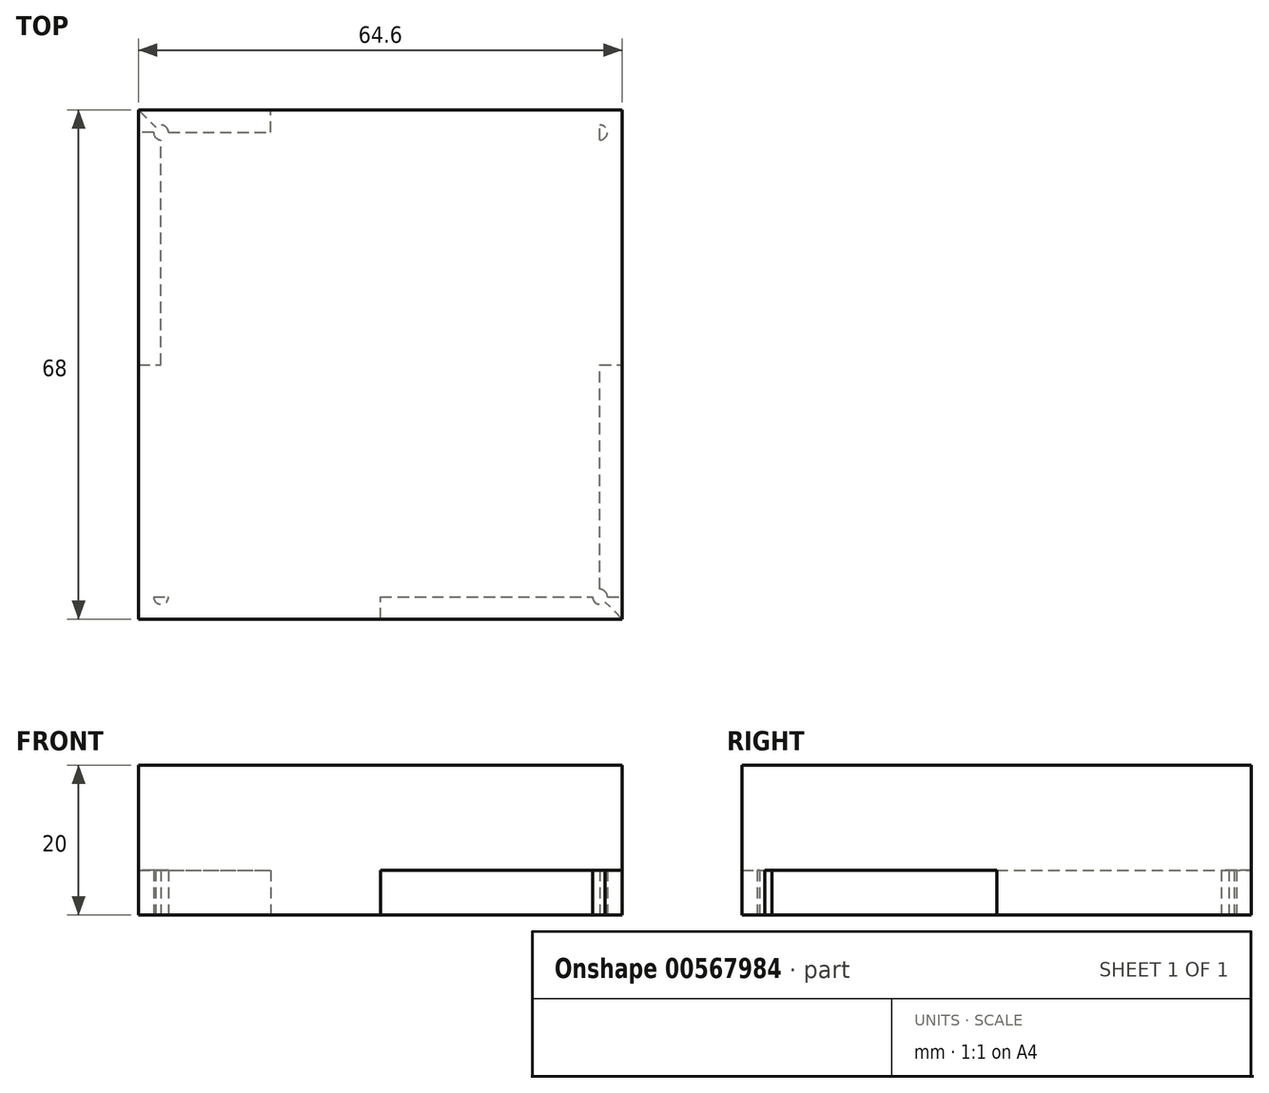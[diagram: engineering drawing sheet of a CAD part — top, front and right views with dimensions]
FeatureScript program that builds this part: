
annotation { "Feature Type Name" : "Feature", "Feature Type Description" : "" }
export const myFeature = defineFeature(function(context is Context, id is Id, definition is map)
    precondition{}
    {
        {
            var Q0;
            Q0=qCreatedBy(makeId("Top.planeOp"),FACE);
            var sketch = newSketch(context, id + "F0", { "sketchPlane" : qUnion([Q0])});
            skLineSegment(sketch, "E0.bottom", {"start": v(-13.19, -10) * mm, "end": v(51.41, -10) * mm});
            skLineSegment(sketch, "E0.top", {"start": v(-13.19, 58) * mm, "end": v(51.41, 58) * mm});
            skLineSegment(sketch, "E0.left", {"start": v(-13.19, -10) * mm, "end": v(-13.19, 58) * mm});
            skLineSegment(sketch, "E0.right", {"start": v(51.41, -10) * mm, "end": v(51.41, 58) * mm});
            skSolve(sketch);
        }
        {
            var Q0;
            Q0=makeQuery(id+"F0.imprint","IMPRINT",FACE,{"disambiguationData":[TD([[makeQuery(id+"F0.imprint","IMPRINT",EDGE,{"derivedFrom":sQuery(id+"F0.wireOp",EDGE,"E0.bottom")}),1.0]])]});
            extrude(context, id + "F1", {"entities" : qUnion([Q0]), "depth" : 20 * mm, "offsetDistance" : 25 * mm});
        }
        {
            var Q0;
            Q0=makeQuery(id+"F1.opExtrude","CAP_FACE",FACE,{"disambiguationData":[OSD([sQuery(id+"F0.wireOp",EDGE,"E0.bottom"),sQuery(id+"F0.wireOp",EDGE,"E0.top"),sQuery(id+"F0.wireOp",EDGE,"E0.left"),sQuery(id+"F0.wireOp",EDGE,"E0.right")])],"isStart":true});
            var sketch = newSketch(context, id + "F2", { "sketchPlane" : qUnion([Q0])});
            skCircle(sketch, "E1", {"center": v(-10.19, 7) * mm, "radius": 1 * mm});
            skLineSegment(sketch, "E2", {"start": v(-13.19, 10) * mm, "end": v(-10.19, 7) * mm});
            skLineSegment(sketch, "E3", {"start": v(-10.19, 7) * mm, "end": v(-13.19, 7) * mm});
            skLineSegment(sketch, "E4", {"start": v(-10.19, 7) * mm, "end": v(-10.19, 10) * mm});
            skLineSegment(sketch, "E5", {"start": v(19.11, 10) * mm, "end": v(19.11, -58) * mm});
            skLineSegment(sketch, "E6", {"start": v(-13.19, -24) * mm, "end": v(51.41, -24) * mm});
            skCircle(sketch, "E7.MirrorC", {"center": v(48.41, 7) * mm, "radius": 1 * mm});
            skLineSegment(sketch, "E8.MirrorCS", {"start": v(48.41, 7) * mm, "end": v(51.41, 7) * mm});
            skLineSegment(sketch, "E9.MirrorCS", {"start": v(48.41, 7) * mm, "end": v(48.41, 10) * mm});
            skLineSegment(sketch, "E10.MirrorCS", {"start": v(51.41, 10) * mm, "end": v(48.41, 7) * mm});
            skLineSegment(sketch, "E11.MirrorCS", {"start": v(-13.19, -58) * mm, "end": v(-10.19, -55) * mm});
            skCircle(sketch, "E12.MirrorC", {"center": v(-10.19, -55) * mm, "radius": 1 * mm});
            skLineSegment(sketch, "E13.MirrorCS", {"start": v(-10.19, -55) * mm, "end": v(-10.19, -58) * mm});
            skLineSegment(sketch, "E14.MirrorCS", {"start": v(-10.19, -55) * mm, "end": v(-13.19, -55) * mm});
            skLineSegment(sketch, "E15.MirrorCS", {"start": v(51.41, -58) * mm, "end": v(48.41, -55) * mm});
            skLineSegment(sketch, "E16.MirrorCS", {"start": v(48.41, -55) * mm, "end": v(51.41, -55) * mm});
            skLineSegment(sketch, "E17.MirrorCS", {"start": v(48.41, -55) * mm, "end": v(48.41, -58) * mm});
            skCircle(sketch, "E18.MirrorC", {"center": v(48.41, -55) * mm, "radius": 1 * mm});
            skLineSegment(sketch, "E19.bottom", {"start": v(-10.19, 7) * mm, "end": v(48.41, 7) * mm});
            skLineSegment(sketch, "E19.top", {"start": v(-10.19, -55) * mm, "end": v(48.41, -55) * mm});
            skLineSegment(sketch, "E19.left", {"start": v(-10.19, 7) * mm, "end": v(-10.19, -55) * mm});
            skLineSegment(sketch, "E19.right", {"start": v(48.41, 7) * mm, "end": v(48.41, -55) * mm});
            skLineSegment(sketch, "E20", {"start": v(48.41, -39.5) * mm, "end": v(-10.19, -39.5) * mm});
            skLineSegment(sketch, "E21", {"start": v(48.41, -39.5) * mm, "end": v(48.41, -55) * mm});
            skLineSegment(sketch, "E22", {"start": v(48.41, -8.5) * mm, "end": v(-10.19, -8.5) * mm});
            skLineSegment(sketch, "E23", {"start": v(33.76, 7) * mm, "end": v(33.76, -55) * mm});
            skLineSegment(sketch, "E24", {"start": v(4.46, 7) * mm, "end": v(4.46, -58) * mm});
            skLineSegment(sketch, "E25.bottom", {"start": v(4.46, -8.5) * mm, "end": v(33.76, -8.5) * mm});
            skLineSegment(sketch, "E25.top", {"start": v(4.46, -39.5) * mm, "end": v(33.76, -39.5) * mm});
            skLineSegment(sketch, "E25.left", {"start": v(4.46, -8.5) * mm, "end": v(4.46, -39.5) * mm});
            skLineSegment(sketch, "E25.right", {"start": v(33.76, -8.5) * mm, "end": v(33.76, -39.5) * mm});
            skLineSegment(sketch, "E26.bottom", {"start": v(33.76, -39.5) * mm, "end": v(19.11, -39.5) * mm});
            skLineSegment(sketch, "E26.top", {"start": v(33.76, -24) * mm, "end": v(19.11, -24) * mm});
            skLineSegment(sketch, "E26.left", {"start": v(33.76, -39.5) * mm, "end": v(33.76, -24) * mm});
            skLineSegment(sketch, "E26.right", {"start": v(19.11, -39.5) * mm, "end": v(19.11, -24) * mm});
            skSolve(sketch);
        }
        {
            var Q0;
            {var subQ0=sQuery(id+"F2.wireOp",EDGE,"E9.MirrorCS");var subQ1=sQuery(id+"F2.wireOp",EDGE,"E7.MirrorC");var subQ2=makeQuery(id+"F2.imprint","INTERSECT",VERTEX,{"derivedFrom":[subQ1,subQ0]});Q0=makeQuery(id+"F2.imprint","IMPRINT",FACE,{"disambiguationData":[TD([[makeQuery(id+"F2.imprint","IMPRINT",EDGE,{"disambiguationData":[TD([[subQ2,1.0]])],"derivedFrom":subQ1}),-1.0]])]});}
            var Q1;
            {var subQ0=sQuery(id+"F2.wireOp",EDGE,"E9.MirrorCS");var subQ1=sQuery(id+"F2.wireOp",EDGE,"E7.MirrorC");var subQ2=makeQuery(id+"F2.imprint","INTERSECT",VERTEX,{"derivedFrom":[subQ1,subQ0]});Q1=makeQuery(id+"F2.imprint","IMPRINT",FACE,{"disambiguationData":[TD([[makeQuery(id+"F2.imprint","IMPRINT",EDGE,{"disambiguationData":[TD([[subQ2,-1.0]])],"derivedFrom":subQ1}),-1.0]])]});}
            var Q2;
            {var subQ0=sQuery(id+"F2.wireOp",EDGE,"E8.MirrorCS");var subQ1=sQuery(id+"F2.wireOp",EDGE,"E7.MirrorC");var subQ2=makeQuery(id+"F2.imprint","INTERSECT",VERTEX,{"derivedFrom":[subQ1,subQ0]});Q2=makeQuery(id+"F2.imprint","IMPRINT",FACE,{"disambiguationData":[TD([[makeQuery(id+"F2.imprint","IMPRINT",EDGE,{"disambiguationData":[TD([[subQ2,1.0]])],"derivedFrom":subQ1}),-1.0]])]});}
            var Q3;
            {var subQ1=sQuery(id+"F2.wireOp",EDGE,"E16.MirrorCS");var subQ3=sQuery(id+"F2.wireOp",EDGE,"E18.MirrorC");var subQ4=makeQuery(id+"F2.imprint","INTERSECT",VERTEX,{"derivedFrom":[subQ1,subQ3]});Q3=makeQuery(id+"F2.imprint","IMPRINT",FACE,{"disambiguationData":[TD([[makeQuery(id+"F2.imprint","IMPRINT",EDGE,{"disambiguationData":[TD([[subQ4,-1.0]])],"derivedFrom":subQ3}),1.0]])]});}
            var Q4;
            {var subQ0=sQuery(id+"F2.wireOp",EDGE,"E16.MirrorCS");var subQ3=sQuery(id+"F2.wireOp",EDGE,"E18.MirrorC");var subQ5=makeQuery(id+"F2.imprint","INTERSECT",VERTEX,{"derivedFrom":[subQ0,subQ3]});Q4=makeQuery(id+"F2.imprint","IMPRINT",FACE,{"disambiguationData":[TD([[makeQuery(id+"F2.imprint","IMPRINT",EDGE,{"disambiguationData":[TD([[subQ5,1.0]])],"derivedFrom":subQ3}),1.0]])]});}
            var Q5;
            {var subQ0=sQuery(id+"F2.wireOp",EDGE,"E17.MirrorCS");var subQ3=sQuery(id+"F2.wireOp",EDGE,"E18.MirrorC");var subQ5=makeQuery(id+"F2.imprint","INTERSECT",VERTEX,{"derivedFrom":[subQ0,subQ3]});Q5=makeQuery(id+"F2.imprint","IMPRINT",FACE,{"disambiguationData":[TD([[makeQuery(id+"F2.imprint","IMPRINT",EDGE,{"disambiguationData":[TD([[subQ5,-1.0]])],"derivedFrom":subQ3}),1.0]])]});}
            var Q6;
            {var subQ0=sQuery(id+"F2.wireOp",EDGE,"E4");var subQ1=sQuery(id+"F2.wireOp",EDGE,"E1");var subQ2=makeQuery(id+"F2.imprint","INTERSECT",VERTEX,{"derivedFrom":[subQ1,subQ0]});Q6=makeQuery(id+"F2.imprint","IMPRINT",FACE,{"disambiguationData":[TD([[makeQuery(id+"F2.imprint","IMPRINT",EDGE,{"disambiguationData":[TD([[subQ2,1.0]])],"derivedFrom":subQ1}),1.0]])]});}
            var Q7;
            {var subQ0=sQuery(id+"F2.wireOp",EDGE,"E4");var subQ1=sQuery(id+"F2.wireOp",EDGE,"E1");var subQ2=makeQuery(id+"F2.imprint","INTERSECT",VERTEX,{"derivedFrom":[subQ1,subQ0]});Q7=makeQuery(id+"F2.imprint","IMPRINT",FACE,{"disambiguationData":[TD([[makeQuery(id+"F2.imprint","IMPRINT",EDGE,{"disambiguationData":[TD([[subQ2,-1.0]])],"derivedFrom":subQ1}),1.0]])]});}
            var Q8;
            {var subQ0=sQuery(id+"F2.wireOp",EDGE,"E3");var subQ1=sQuery(id+"F2.wireOp",EDGE,"E1");var subQ2=makeQuery(id+"F2.imprint","INTERSECT",VERTEX,{"derivedFrom":[subQ1,subQ0]});Q8=makeQuery(id+"F2.imprint","IMPRINT",FACE,{"disambiguationData":[TD([[makeQuery(id+"F2.imprint","IMPRINT",EDGE,{"disambiguationData":[TD([[subQ2,1.0]])],"derivedFrom":subQ1}),1.0]])]});}
            var Q9;
            {var subQ0=sQuery(id+"F2.wireOp",EDGE,"E13.MirrorCS");var subQ1=sQuery(id+"F2.wireOp",EDGE,"E12.MirrorC");var subQ2=makeQuery(id+"F2.imprint","INTERSECT",VERTEX,{"derivedFrom":[subQ1,subQ0]});Q9=makeQuery(id+"F2.imprint","IMPRINT",FACE,{"disambiguationData":[TD([[makeQuery(id+"F2.imprint","IMPRINT",EDGE,{"disambiguationData":[TD([[subQ2,1.0]])],"derivedFrom":subQ1}),-1.0]])]});}
            var Q10;
            {var subQ0=sQuery(id+"F2.wireOp",EDGE,"E13.MirrorCS");var subQ3=sQuery(id+"F2.wireOp",EDGE,"E12.MirrorC");var subQ5=makeQuery(id+"F2.imprint","INTERSECT",VERTEX,{"derivedFrom":[subQ3,subQ0]});Q10=makeQuery(id+"F2.imprint","IMPRINT",FACE,{"disambiguationData":[TD([[makeQuery(id+"F2.imprint","IMPRINT",EDGE,{"disambiguationData":[TD([[subQ5,-1.0]])],"derivedFrom":subQ3}),-1.0]])]});}
            var Q11;
            {var subQ0=sQuery(id+"F2.wireOp",EDGE,"E14.MirrorCS");var subQ3=sQuery(id+"F2.wireOp",EDGE,"E12.MirrorC");var subQ5=makeQuery(id+"F2.imprint","INTERSECT",VERTEX,{"derivedFrom":[subQ3,subQ0]});Q11=makeQuery(id+"F2.imprint","IMPRINT",FACE,{"disambiguationData":[TD([[makeQuery(id+"F2.imprint","IMPRINT",EDGE,{"disambiguationData":[TD([[subQ5,1.0]])],"derivedFrom":subQ3}),-1.0]])]});}
            extrude(context, id + "F3", {"entities" : qUnion([Q0, Q1, Q2, Q3, Q4, Q5, Q6, Q7, Q8, Q9, Q10, Q11]), "operationType" : NewBodyOperationType.REMOVE, "oppositeDirection" : true, "depth" : 6 * mm, "offsetDistance" : 25 * mm});
        }
    });
